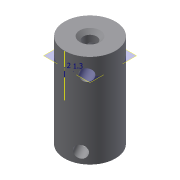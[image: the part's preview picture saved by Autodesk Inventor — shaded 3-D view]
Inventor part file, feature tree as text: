
AUTODESK INVENTOR PART (.ipt)
format: ipt  version: 2022 (Build 260153000, 153)  size: 201,216 bytes
history: native  units: mm
features: sketch x5, extrude x4, plane x1, pattern_circular x1, chamfer x1
ambient origin geometry x8: Origin, YZ Plane, XZ Plane, XY Plane, X Axis, Y Axis, Z Axis, Center Point
bodies: Solid1 (feature_tree)
feature tree (12):
  extrude  "Extrusion1"  Depth=10.0mm TaperAngle=0.0deg
  extrude  "Extrusion2"  Depth=2.2mm
  plane  "Work Plane1"
  sketch  "Sketch5"  dims[d6=12.0mm d7=0.0mm d14=-6.0mm]
  extrude  "Extrusion5"  [1 undecoded]
  pattern_circular  "Circular Pattern3"  [2 undecoded]
  chamfer  "Chamfer4"  Distance=2.8mm
  extrude  "Extrusion6"  Depth=10.0mm
  sketch  "Sketch1"  dims[d0=12.0mm d2=10.0mm d3=0.0mm]
  sketch  "Sketch2"  dims[d4=5.1mm d5=2.2mm]
  sketch  "Sketch6"  dims[d17=1.3mm]
  sketch  "Sketch7"  dims[d18=2.0mm d42=2.8mm d43=2.8mm d44=7.0mm d45=10.0mm d46=0.0mm d47=30.0mm d48=360.0deg d50=1.0mm d51=2.0mm d52=45.0deg d53=3.2mm d54=10.0mm d55=-0.349066mm d56=2.8mm]
note: 3 required parameter values undecoded (feature->parameter linkage not recoverable at this tier; creation-order binding heuristic only, values carry confidence <= 0.55)
